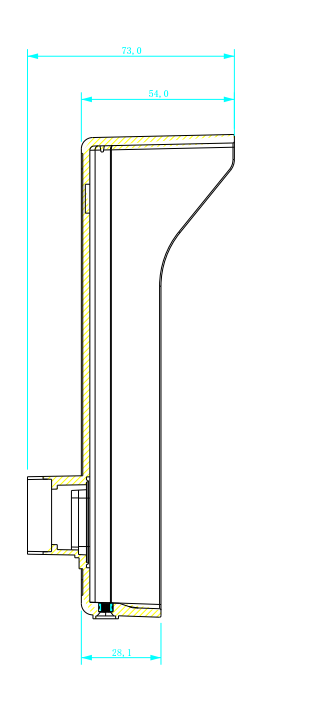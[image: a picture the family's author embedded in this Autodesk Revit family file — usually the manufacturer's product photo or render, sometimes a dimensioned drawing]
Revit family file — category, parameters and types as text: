
# Revit family: BR-AA12
name_source: partatom
category: Устройства связи
units: mm (PartAtom-declared; Revit-internal decimal feet)

## family parameters
Всегда вертикально = Нет
На основе рабочей плоскости = Да
Общий = Да
При загрузке вырезать с полостями = Нет
Размер круглого соединителя = Использовать диаметр
Сохранять ориентацию аннотаций = Нет
Тип детали = Нормальный
Точка принадлежности помещению = Нет

## types (1)
- BR-AA12
    ADSK_URL документации изделия = -
    ADSK_URL страницы изделия = https://www.bas-ip.ru
    ADSK_Версия Revit = Revit 2020
    ADSK_Единица измерения = шт
    ADSK_Завод-изготовитель = BAS-IP
    ADSK_Марка = BR-AA12
    ADSK_Наименование = Кронштейн для накладного монтажа с козырьком BR-AA12
    ADSK_Наименование краткое = BR-AA12
    ADSK_Размер_Длина = 387 мм
    ADSK_Размер_Толщина = 107 мм
    ADSK_Размер_Ширина = 164 мм
    BIM library = https://bimlib.ru
    URL = https://www.bas-ip.ru
    Группа модели = Кронштейн для накладного монтажа с козырьком BR-AA12
    Изготовитель = BAS-IP
    Изображение типоразмера = <Нет>
    Корпус = Металлический
    Материал корпуса = Материал черный
    Описание = Кронштейн с козырьком для накладного монтажа для многоквартирных панелей AА-12B
    Отметка по умолчанию = 0 мм
    Размеры = 164кх387х107 мм
    Цветовое решение = Gold, Silver, Black
